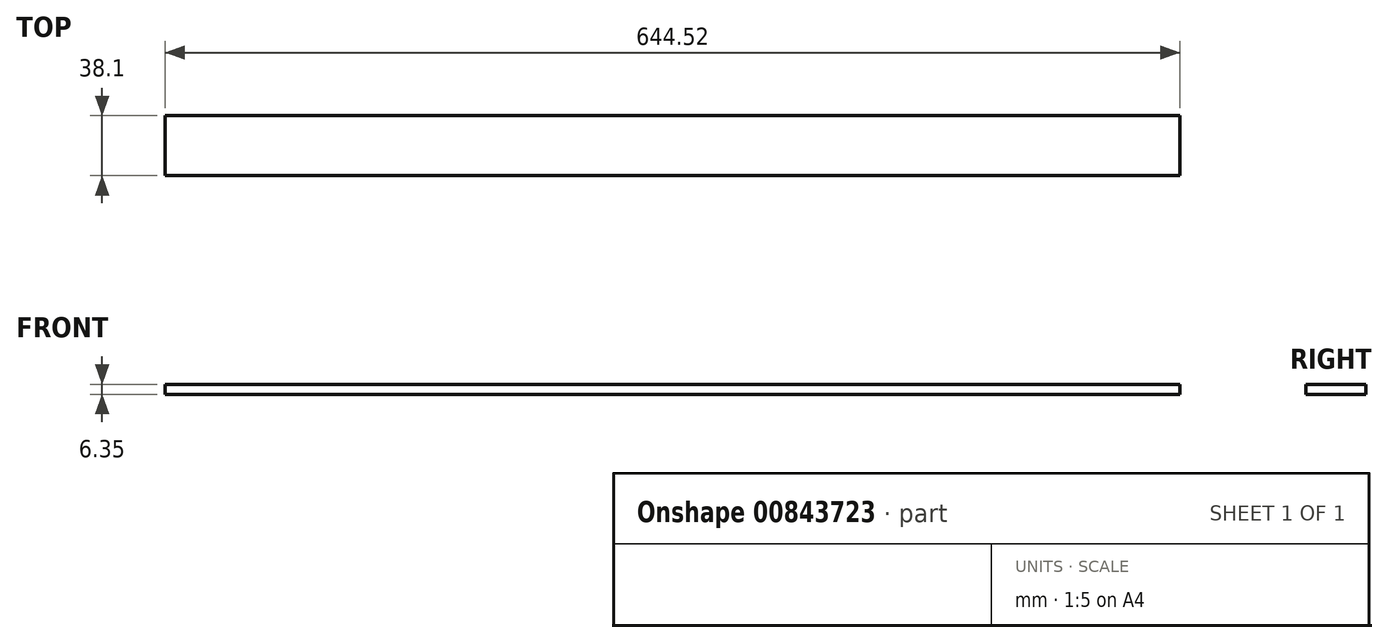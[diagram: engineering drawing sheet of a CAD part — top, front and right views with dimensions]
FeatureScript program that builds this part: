
annotation { "Feature Type Name" : "Feature", "Feature Type Description" : "" }
export const myFeature = defineFeature(function(context is Context, id is Id, definition is map)
    precondition{}
    {
        {
            var Q0;
            Q0=qCreatedBy(makeId("Top.planeOp"),FACE);
            var sketch = newSketch(context, id + "F0", { "sketchPlane" : qUnion([Q0])});
            skLineSegment(sketch, "E0.bottom", {"start": v(322.26, 19.05) * mm, "end": v(-322.26, 19.05) * mm});
            skLineSegment(sketch, "E0.top", {"start": v(322.26, -19.05) * mm, "end": v(-322.26, -19.05) * mm});
            skLineSegment(sketch, "E0.left", {"start": v(322.26, 19.05) * mm, "end": v(322.26, -19.05) * mm});
            skLineSegment(sketch, "E0.right", {"start": v(-322.26, 19.05) * mm, "end": v(-322.26, -19.05) * mm});
            skPoint(sketch, "E0.middle", {"position": v(0, 0) * mm});
            skSolve(sketch);
        }
        {
            var Q0;
            Q0 = qSketchRegion(id + "F0", true);
            extrude(context, id + "F1", {"entities" : qUnion([Q0]), "depth" : 6.35 * mm, "offsetDistance" : 25.4 * mm});
        }
    });
